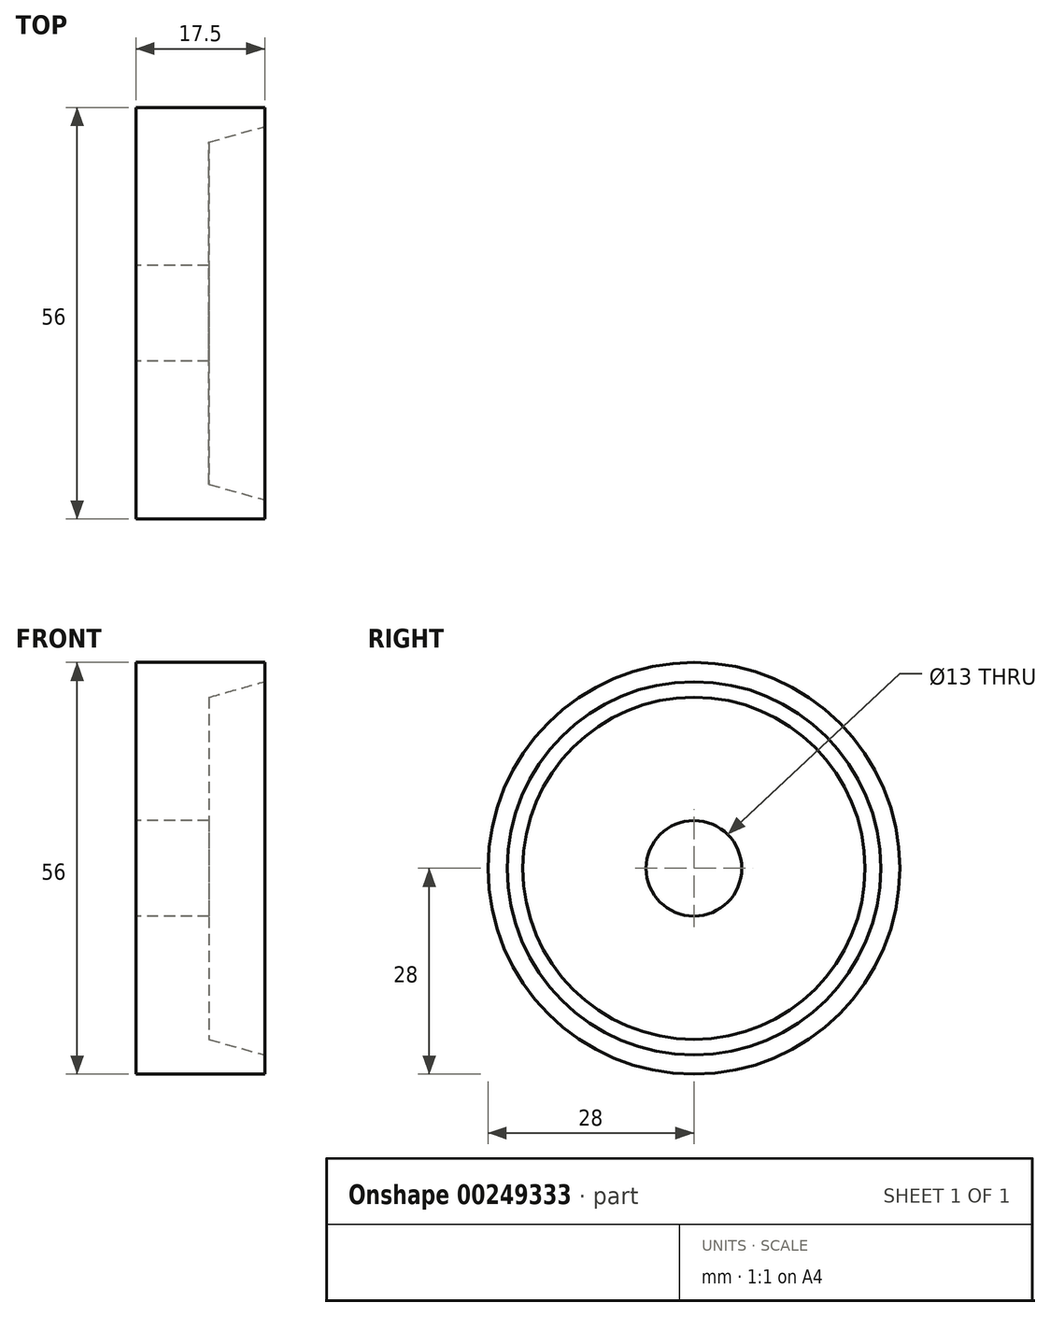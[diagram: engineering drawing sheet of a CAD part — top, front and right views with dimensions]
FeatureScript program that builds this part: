
annotation { "Feature Type Name" : "Feature", "Feature Type Description" : "" }
export const myFeature = defineFeature(function(context is Context, id is Id, definition is map)
    precondition{}
    {
        {
            var Q0;
            Q0=qCreatedBy(makeId("Front.planeOp"),FACE);
            var sketch = newSketch(context, id + "F0", { "sketchPlane" : qUnion([Q0])});
            skLineSegment(sketch, "E0", {"start": v(-12.55, 0) * mm, "end": v(0, 0) * mm, "construction": true});
            skLineSegment(sketch, "E1", {"start": v(0, 6.5) * mm, "end": v(0, 23.83) * mm, "construction": true});
            skLineSegment(sketch, "E2", {"start": v(0, 23.83) * mm, "end": v(5.6, 25.4) * mm, "construction": true});
            skLineSegment(sketch, "E3", {"start": v(5.6, 25.4) * mm, "end": v(5.6, 28) * mm});
            skLineSegment(sketch, "E4", {"start": v(5.6, 28) * mm, "end": v(-11.9, 28) * mm});
            skLineSegment(sketch, "E5", {"start": v(-11.9, 28) * mm, "end": v(-11.9, 6.5) * mm});
            skLineSegment(sketch, "E6", {"start": v(-2, 6.5) * mm, "end": v(-11.9, 6.5) * mm});
            skLineSegment(sketch, "E7", {"start": v(0, 23.83) * mm, "end": v(12.27, 23.83) * mm, "construction": true});
            skLineSegment(sketch, "E8", {"start": v(5.6, 25.4) * mm, "end": v(-2, 23.27) * mm});
            skLineSegment(sketch, "E9", {"start": v(-2, 23.27) * mm, "end": v(-2, 6.5) * mm});
            skSolve(sketch);
        }
        {
            var Q0;
            Q0=makeQuery(id+"F0.imprint","IMPRINT",FACE,{"disambiguationData":[TD([[makeQuery(id+"F0.imprint","IMPRINT",EDGE,{"derivedFrom":sQuery(id+"F0.wireOp",EDGE,"E3")}),1.0]])]});
            var Q1;
            Q1=sQuery(id+"F0.wireOp",EDGE,"E0");
            revolve(context, id + "F1", {"entities" : qUnion([Q0]), "axis" : qUnion([Q1]), "revolveType" : RevolveType.FULL});
        }
    });
